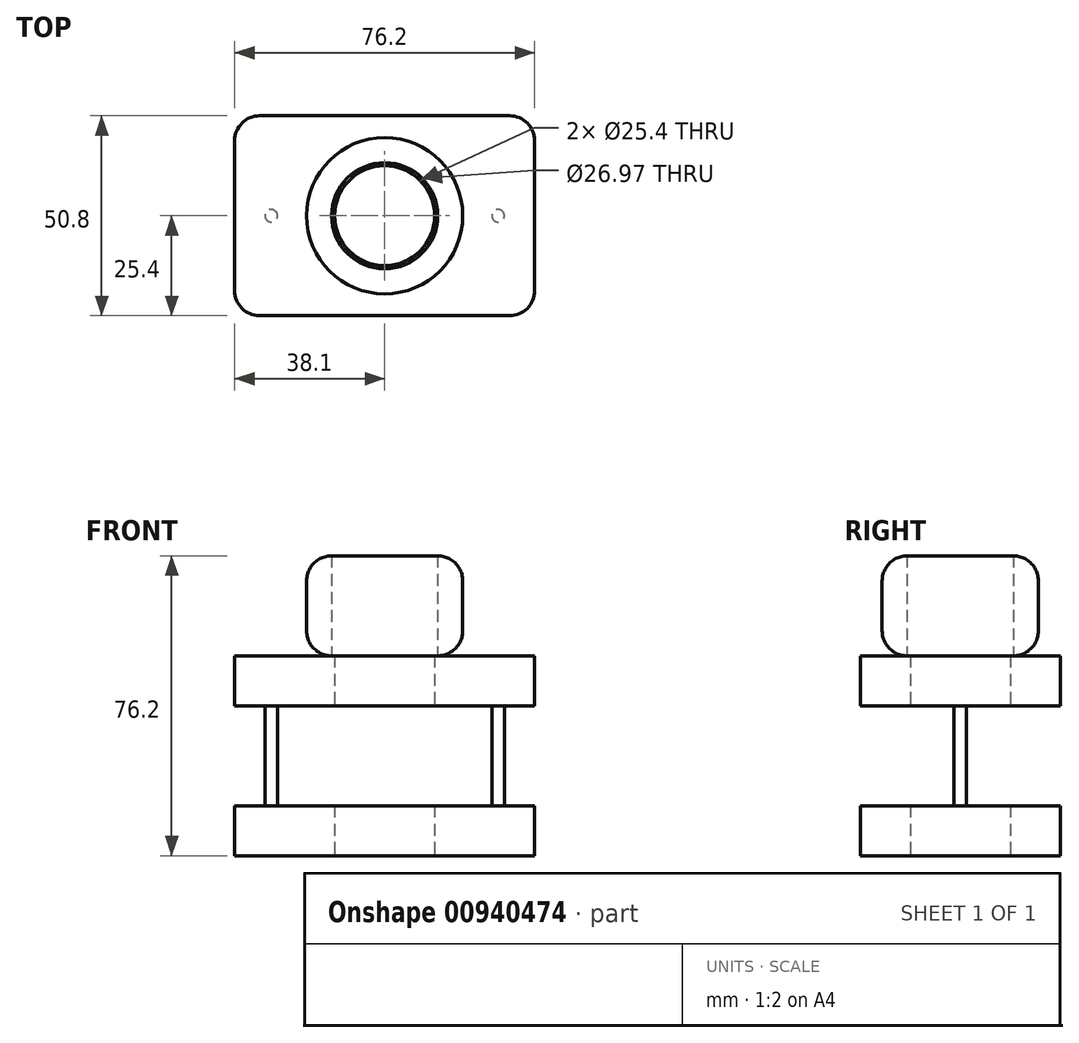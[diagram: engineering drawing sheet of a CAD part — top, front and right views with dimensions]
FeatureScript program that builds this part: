
annotation { "Feature Type Name" : "Feature", "Feature Type Description" : "" }
export const myFeature = defineFeature(function(context is Context, id is Id, definition is map)
    precondition{}
    {
        {
            var Q0;
            Q0=qCreatedBy(makeId("Top.planeOp"),FACE);
            var sketch = newSketch(context, id + "F0", { "sketchPlane" : qUnion([Q0])});
            skLineSegment(sketch, "E0.bottom", {"start": v(-38.1, -25.4) * mm, "end": v(38.1, -25.4) * mm});
            skLineSegment(sketch, "E0.top", {"start": v(-38.1, 25.4) * mm, "end": v(38.1, 25.4) * mm});
            skLineSegment(sketch, "E0.left", {"start": v(-38.1, -25.4) * mm, "end": v(-38.1, 25.4) * mm});
            skLineSegment(sketch, "E0.right", {"start": v(38.1, -25.4) * mm, "end": v(38.1, 25.4) * mm});
            skPoint(sketch, "E0.middle", {"position": v(0, 0) * mm});
            skCircle(sketch, "E1", {"center": v(0, 0) * mm, "radius": 12.7 * mm});
            skSolve(sketch);
        }
        {
            var Q0;
            Q0 = qSketchRegion(id + "F0", true);
            extrude(context, id + "F1", {"entities" : qUnion([Q0]), "depth" : 12.7 * mm, "offsetDistance" : 25.4 * mm});
        }
        {
            var Q0;
            Q0=makeQuery(id+"F1.opExtrude","SWEPT_EDGE",EDGE,{"disambiguationData":[OSD([sQuery(id+"F0.wireOp",EDGE,"E0.bottom"),sQuery(id+"F0.wireOp",EDGE,"E0.right")])]});
            var Q1;
            Q1=makeQuery(id+"F1.opExtrude","SWEPT_EDGE",EDGE,{"disambiguationData":[OSD([sQuery(id+"F0.wireOp",EDGE,"E0.top"),sQuery(id+"F0.wireOp",EDGE,"E0.right")])]});
            var Q2;
            Q2=makeQuery(id+"F1.opExtrude","SWEPT_EDGE",EDGE,{"disambiguationData":[OSD([sQuery(id+"F0.wireOp",EDGE,"E0.bottom"),sQuery(id+"F0.wireOp",EDGE,"E0.left")])]});
            var Q3;
            Q3=makeQuery(id+"F1.opExtrude","SWEPT_EDGE",EDGE,{"disambiguationData":[OSD([sQuery(id+"F0.wireOp",EDGE,"E0.top"),sQuery(id+"F0.wireOp",EDGE,"E0.left")])]});
            fillet(context, id + "F2", {"entities" : qUnion([Q0, Q1, Q2, Q3]), "radius" : 6.35 * mm, "tangentPropagation" : true, "allowEdgeOverflow" : false});
        }
        {
            var Q0;
            Q0=makeQuery(id+"F1.opExtrude","CAP_FACE",FACE,{"disambiguationData":[OSD([sQuery(id+"F0.wireOp",EDGE,"E0.bottom"),sQuery(id+"F0.wireOp",EDGE,"E0.top"),sQuery(id+"F0.wireOp",EDGE,"E0.left"),sQuery(id+"F0.wireOp",EDGE,"E0.right"),sQuery(id+"F0.wireOp",EDGE,"E1")])],"isStart":false});
            var sketch = newSketch(context, id + "F3", { "sketchPlane" : qUnion([Q0])});
            skCircle(sketch, "E2", {"center": v(-28.81, 0) * mm, "radius": 1.59 * mm});
            skLineSegment(sketch, "E3", {"start": v(0, -17.72) * mm, "end": v(0, 20.1) * mm, "construction": true});
            skCircle(sketch, "E4.MirrorC", {"center": v(28.81, 0) * mm, "radius": 1.59 * mm});
            skSolve(sketch);
        }
        {
            var Q0;
            Q0 = qSketchRegion(id + "F3", true);
            extrude(context, id + "F4", {"entities" : qUnion([Q0]), "operationType" : NewBodyOperationType.ADD, "depth" : 25.4 * mm, "offsetDistance" : 25.4 * mm});
        }
        {
            var Q0;
            Q0=makeQuery(id+"F4.opExtrude","CAP_FACE",FACE,{"disambiguationData":[OSD([sQuery(id+"F3.wireOp",EDGE,"E2")])],"isStart":false});
            var sketch = newSketch(context, id + "F5", { "sketchPlane" : qUnion([Q0])});
            skLineSegment(sketch, "E5.0", {"start": v(-38.1, -19.05) * mm, "end": v(-38.1, 19.05) * mm});
            skArc(sketch, "E5.1", {"start": v(-31.75, 25.4) * mm, "mid": v(-36.24, 23.54) * mm, "end": v(-38.1, 19.05) * mm});
            skLineSegment(sketch, "E5.2", {"start": v(-31.75, 25.4) * mm, "end": v(31.75, 25.4) * mm});
            skArc(sketch, "E5.3", {"start": v(38.1, 19.05) * mm, "mid": v(36.24, 23.54) * mm, "end": v(31.75, 25.4) * mm});
            skLineSegment(sketch, "E5.4", {"start": v(38.1, -19.05) * mm, "end": v(38.1, 19.05) * mm});
            skArc(sketch, "E5.5", {"start": v(31.75, -25.4) * mm, "mid": v(36.24, -23.54) * mm, "end": v(38.1, -19.05) * mm});
            skLineSegment(sketch, "E5.6", {"start": v(-31.75, -25.4) * mm, "end": v(31.75, -25.4) * mm});
            skArc(sketch, "E5.7", {"start": v(-38.1, -19.05) * mm, "mid": v(-36.24, -23.54) * mm, "end": v(-31.75, -25.4) * mm});
            skPoint(sketch, "E5.8", {"position": v(-36.24, -23.54) * mm});
            skCircle(sketch, "E6.0", {"center": v(0, 0) * mm, "radius": 12.7 * mm});
            skSolve(sketch);
        }
        {
            var Q0;
            Q0 = qSketchRegion(id + "F5", true);
            extrude(context, id + "F6", {"entities" : qUnion([Q0]), "operationType" : NewBodyOperationType.ADD, "depth" : 12.7 * mm, "offsetDistance" : 25.4 * mm});
        }
        {
            var Q0;
            Q0=qCreatedBy(makeId("Front.planeOp"),FACE);
            var sketch = newSketch(context, id + "F7", { "sketchPlane" : qUnion([Q0])});
            skLineSegment(sketch, "E7.bottom", {"start": v(-19.84, 76.2) * mm, "end": v(-13.49, 76.2) * mm});
            skLineSegment(sketch, "E7.top", {"start": v(-19.84, 50.8) * mm, "end": v(-13.49, 50.8) * mm});
            skLineSegment(sketch, "E7.left", {"start": v(-19.84, 76.2) * mm, "end": v(-19.84, 50.8) * mm});
            skLineSegment(sketch, "E7.right", {"start": v(-13.49, 76.2) * mm, "end": v(-13.49, 50.8) * mm});
            skLineSegment(sketch, "E8", {"start": v(0, 0) * mm, "end": v(0, 81.2) * mm, "construction": true});
            skSolve(sketch);
        }
        {
            var Q0;
            Q0 = qSketchRegion(id + "F7", true);
            var Q1;
            Q1=sQuery(id+"F7.wireOp",EDGE,"E8");
            revolve(context, id + "F8", {"surfaceOperationType" : NewSurfaceOperationType.NEW, "entities" : qUnion([Q0]), "axis" : qUnion([Q1]), "revolveType" : RevolveType.FULL});
        }
        {
            var Q0;
            Q0=makeQuery(id+"F8.opRevolve","SWEPT_EDGE",EDGE,{"disambiguationData":[OSD([sQuery(id+"F7.wireOp",EDGE,"E7.bottom"),sQuery(id+"F7.wireOp",EDGE,"E7.left")])]});
            var Q1;
            Q1=makeQuery(id+"F8.opRevolve","SWEPT_EDGE",EDGE,{"disambiguationData":[OSD([sQuery(id+"F7.wireOp",EDGE,"E7.top"),sQuery(id+"F7.wireOp",EDGE,"E7.left")])]});
            fillet(context, id + "F9", {"entities" : qUnion([Q0, Q1]), "radius" : 6.35 * mm, "tangentPropagation" : true, "allowEdgeOverflow" : false});
        }
    });
